# Revit family: 0051032 Sylvania Lighting Fixture LED PIPE G2 L600 NW
name_source: partatom
category: Lighting Fixtures
revit_build: Autodesk Revit 2016 (Build: 20150220_1215(x64)
units: mm (PartAtom-declared; Revit-internal decimal feet)

## family parameters
Cut with Voids When Loaded = No
Host = Face
Light Source = Yes
OmniClass Number = 23.80.70.00
OmniClass Title = Lighting
Part Type = Normal
Room Calculation Point = No
Round Connector Dimension = Use Diameter
Shared = No

## types (1)
- 0051032 LED PIPE G2 L600 NW
    Apparent Load = 7 VA
    Assembly Code = D5020200
    AssetType = Fixed
    ClassificationName = Uniclass2015
    ClassificationValue = EF_70_80
    Color Filter = 16777215
    Cost = 0 $
    Default Elevation = 1219 mm
    Description = LED T5 replacement batten, seamless linking (up to 10M), Ideal for direct lighting such as under cabinet or in kitchens, 150 degree beam angle, includes switch, includes 0.30m stripped cable, white polycarbonate body, includes standard and tilting brackets
    Dimming Lamp Color Temperature Shift = <None>
    DocumentationLiterature = http://www.sylvania-lighting.com
    DurationUnit = hours
    ElectricShockClassification = Class II
    Emit Shape Visible in Rendering = No
    Emit from Rectangle Length = 594 mm
    Emit from Rectangle Width = 10 mm  [stored 0.0328084 ft]
    ExpectedLife = 50000
    Height_SYL = 35 mm  [stored 0.114829 ft]
    IfcExportAs = IfcLightFixtureType
    IfcExportType = IfcLightFixtureType
    ImpactProtectionIndex = IK02
    IngressProtection = IP20
    InputNominalFrequency = 50/60 Hz
    InputVoltage = 220-240V~
    Keynote = 16500
    Lamp = LED
    LampColourRenderingIndex = 80
    LampColourTemperature = 4000 K
    LampMacAdamStep = 6
    LampNominalLuminous = 700 lm
    LampsType = LED
    Length_SYL = 600 mm  [stored 1.9685 ft]
    LuminousEfficacy = 100 lm/W
    Manufacturer = Feilo Sylvania
    ManufacturerName = Feilo Sylvania
    Material = pc housing, pc diffuser
    Material_1_FEILO = Body-Sylvania-ledpipe
    Material_2_FEILO = LED-Sylvania-ledpipe
    Material_3_FEILO = <By Category>
    Material_4_FEILO = <By Category>
    Model = LED PIPE G2 L600 NW
    ModelNumber = 0051032
    ModelReference = LED PIPE G2 L600 NW
    Name = LED PIPE G2 L600 NW
    NominalDepth = 24 mm  [stored 0.0787402 ft]
    NominalHeight = 35 mm  [stored 0.114829 ft]
    NominalLength = 600 mm  [stored 1.9685 ft]
    Photometric Web File = 0051032.ies
    PowerConsumption = 7 W
    PowerFactor = 0.9
    RadiusBottom_SYL = 2 mm  [stored 0.00656168 ft]
    RadiusShoulder_SYL = 5 mm  [stored 0.0164042 ft]
    RadiusSmall_SYL = 1 mm  [stored 0.00328084 ft]
    RadiusTop_SYL = 9 mm
    Tilt Angle = -90.00°
    Type Image = <None>
    TypeName = LED PIPE G2 L600 NW
    URL = http://www.sylvania-lighting.com
    Voltage = 230 V
    Weight = 3.76 kg
    Width_SYL = 24 mm  [stored 0.0787402 ft]

note: [stored X ft] marks values corroborated as IEEE doubles in the binary element streams (Revit-internal decimal feet)

## geometry (parser evidence)
native form markers: Sweep x3
no freeform markers — native parametric forms only
